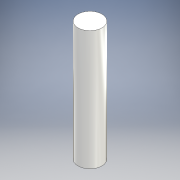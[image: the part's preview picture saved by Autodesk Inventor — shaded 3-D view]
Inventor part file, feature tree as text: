
AUTODESK INVENTOR PART (.ipt)
format: ipt  version: 2016 (Build 200138000, 138)  size: 89,088 bytes
history: native  units: mm
features: other x1, extrude x1, sketch x1
ambient origin geometry x8: Origin, YZ Plane, XZ Plane, XY Plane, X Axis, Y Axis, Z Axis, Center Point
bodies: Body1 (feature_tree)
feature tree (3):
  other  "ソリッド1"
  extrude  "押し出し1"  Depth=4.0mm
  sketch  "スケッチ1"
